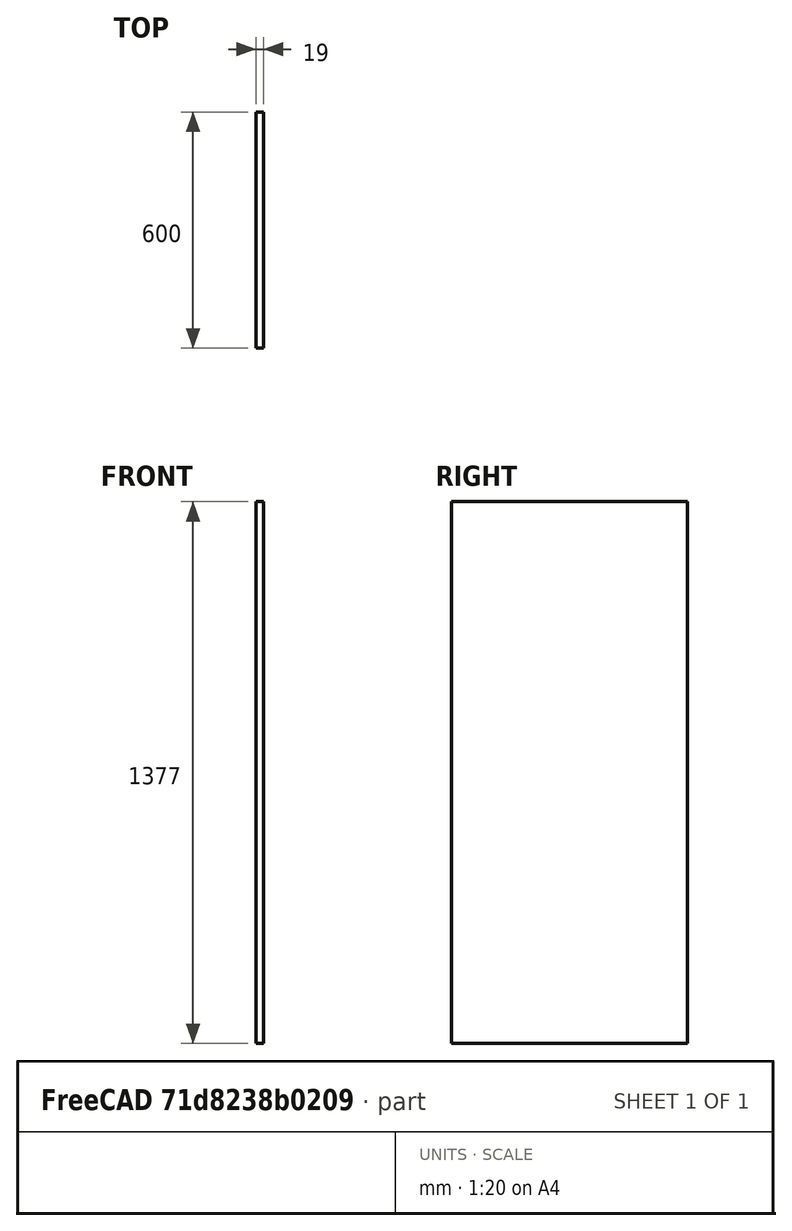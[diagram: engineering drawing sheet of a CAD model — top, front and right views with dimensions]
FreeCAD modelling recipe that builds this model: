
FCSTD DOCUMENT  (FreeCAD 1.0RUnknown)
Label: wardrobe_right_corpus01_jan
License: All rights reserved
LicenseURL: https://en.wikipedia.org/wiki/All_rights_reserved
objects: Sketcher::SketchObject×1, PartDesign::Pad×1, PartDesign::CoordinateSystem×1, PartDesign::Body×1
note: 7 computed .brp shape members not serialized (recipe doc carries the construction recipe); baked Part::Feature solids carry a one-line shape summary decoded from their .brp
EXTERNAL_REF file=../../mastersketch.FCStd obj=Spreadsheet

FEATURE [Sketcher::SketchObject] Sketch002
  ArcFitTolerance = 1e-06
  AttachmentSupport = -> [YZ_Plane004]
  FullyConstrained = true
  MakeInternals = false
  MapMode = 5
  Placement = pos=(0,0,0) rot=(0.57735,0.57735,0.57735;2.0944rad)
  expr: Constraints[10] = mastersketch#Spreadsheet.corpus_depth
  expr: Constraints[11] = mastersketch#Spreadsheet.corpus01_height - 2 * mastersketch#Spreadsheet.corpus_outer_thickness
  sketch-geometry (5):
    g0: LineSegment StartX=-300 StartY=-688.5 StartZ=0 EndX=300 EndY=-688.5 EndZ=0
    g1: LineSegment StartX=300 StartY=-688.5 StartZ=0 EndX=300 EndY=688.5 EndZ=0
    g2: LineSegment StartX=300 StartY=688.5 StartZ=0 EndX=-300 EndY=688.5 EndZ=0
    g3: LineSegment StartX=-300 StartY=688.5 StartZ=0 EndX=-300 EndY=-688.5 EndZ=0
    g4: GeomPoint [constr] X=0 Y=0 Z=0
  constraints (12):
    c: Coincident(g0,g1)
    c: Coincident(g1,g2)
    c: Coincident(g2,g3)
    c: Coincident(g3,g0)
    c: Horizontal(g0)
    c: Horizontal(g2)
    c: Vertical(g1)
    c: Vertical(g3)
    c: Symmetric(g2,g0,g4)
    c: Coincident(g4,g-1)
    c: DistanceX(g0,g0) = 600
    c: DistanceY(g3,g3) = 1377
FEATURE [PartDesign::Pad] Pad002
  Direction = (1,0,0)
  Length = 19
  Length2 = 10
  Placement = pos=(0,0,0) rot=(1,1,1;2.0944rad)
  Profile = -> Sketch002
  ReferenceAxis = -> Sketch002 [N_Axis]
  Refine = true
  Suppressed = false
  Type = 0
  expr: Length = mastersketch#Spreadsheet.corpus_outer_thickness
FEATURE [PartDesign::CoordinateSystem] LCS_bottom
  AttacherType = Attacher::AttachEngine3D
  AttachmentSupport = -> [Pad002]
  MapMode = 45
  Placement = pos=(19,-1.82e-14,-688.5) rot=(0,0.707107,0.707107;3.14159rad)
FEATURE [PartDesign::Body] Body002  label="wardrobe_right_corpus01_jan"
  AllowCompound = false
  Group = -> [Sketch002,Pad002,LCS_bottom]
  Origin = -> Origin004
  Tip = -> Pad002
